# Revit family: VC-LH-1212
name_source: partatom
category: Generic Models
units: mm (PartAtom-declared; Revit-internal decimal feet)

## family parameters
Always vertical = Yes
Can host rebar = No
Cut with Voids When Loaded = Yes
Host = Wall
Maintain Annotation Orientation = No
Part Type = Normal
Room Calculation Point = No
Round Connector Dimension = Use Diameter
Shared = No

## types (9) — shared parameters
BelowFinFloor = 1' - 0 1/2"
Default Elevation = 0' - 0"
Description = Sectional Door
DoorThk = 0' - 4"
HeadRoom = 3' - 0"
Manufacturer = TKO
Model = Verticool
PanelSize = 4' - 0"
PitTrackCutL = 1' - 0"
PitTrackCutW = 1' - 0"
Track Style = Low Headroom 12/12 Pitch
TrackDepth = 0' - 5 3/8"
TrackWidth = 0' - 3 1/2"
Type Comments = Insulated

## per-type parameters (varying)
| type | HorizTrack | OpeningHeight | OpeningWidth | TrackHeight |
| 8' x 10' | 9' - 0 1/2" | 10' - 0 1/2" | 8' - 0" | 13' - 0 1/2" |
| 9' x 10' | 9' - 0 1/2" | 10' - 0 1/2" | 9' - 0" | 13' - 0 1/2" |
| 10' x 10' | 9' - 0 1/2" | 10' - 0 1/2" | 10' - 0" | 13' - 0 1/2" |
| 10' x 11' | 10' - 0 1/2" | 11' - 0 1/2" | 10' - 0" | 14' - 0 1/2" |
| 9' x 11' | 10' - 0 1/2" | 11' - 0 1/2" | 9' - 0" | 14' - 0 1/2" |
| 8' x 11' | 10' - 0 1/2" | 11' - 0 1/2" | 8' - 0" | 14' - 0 1/2" |
| 9' x 12' | 11' - 0 1/2" | 12' - 0 1/2" | 9' - 0" | 15' - 0 1/2" |
| 8' x 12' | 11' - 0 1/2" | 12' - 0 1/2" | 8' - 0" | 15' - 0 1/2" |
| 10' x 12' | 11' - 0 1/2" | 12' - 0 1/2" | 10' - 0" | 15' - 0 1/2" |

## geometry (parser evidence)
native form markers: Sweep x3
no freeform markers — native parametric forms only
